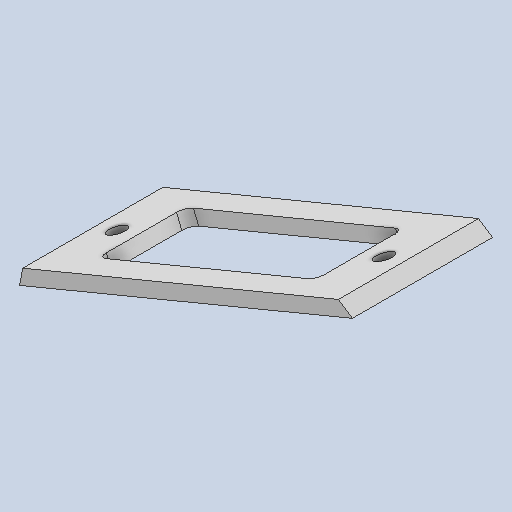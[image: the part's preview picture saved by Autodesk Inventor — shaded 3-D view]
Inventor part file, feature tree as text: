
AUTODESK INVENTOR PART (.ipt)
format: ipt  version: 2025 (Build 290162010, 162A)  size: 129,024 bytes
history: native  units: mm
features: extrude x2, sketch x2, fillet x1
ambient origin geometry x8: Origin, YZ Plane, XZ Plane, XY Plane, X Axis, Y Axis, Z Axis, Center Point
bodies: Solid1 (feature_tree)
feature tree (5):
  extrude  "Extrusion1"  Depth=5.0mm
  extrude  "Extrusion2"  Depth=80.0mm
  fillet  "Fillet1"  [1 undecoded]
  sketch  "Sketch2"  dims[d0=513.0mm d1=260.0mm d2=635.0mm d6=5.0mm]
  sketch  "Sketch3"  dims[d7=8.0mm d8=80.0mm d9=0.0mm d10=135.0mm d11=10.0mm d12=15.0mm d13=50.0mm d14=0.0mm d15=0.0mm d16=5.0mm]
note: 1 required parameter value undecoded (feature->parameter linkage not recoverable at this tier; creation-order binding heuristic only, values carry confidence <= 0.55)
